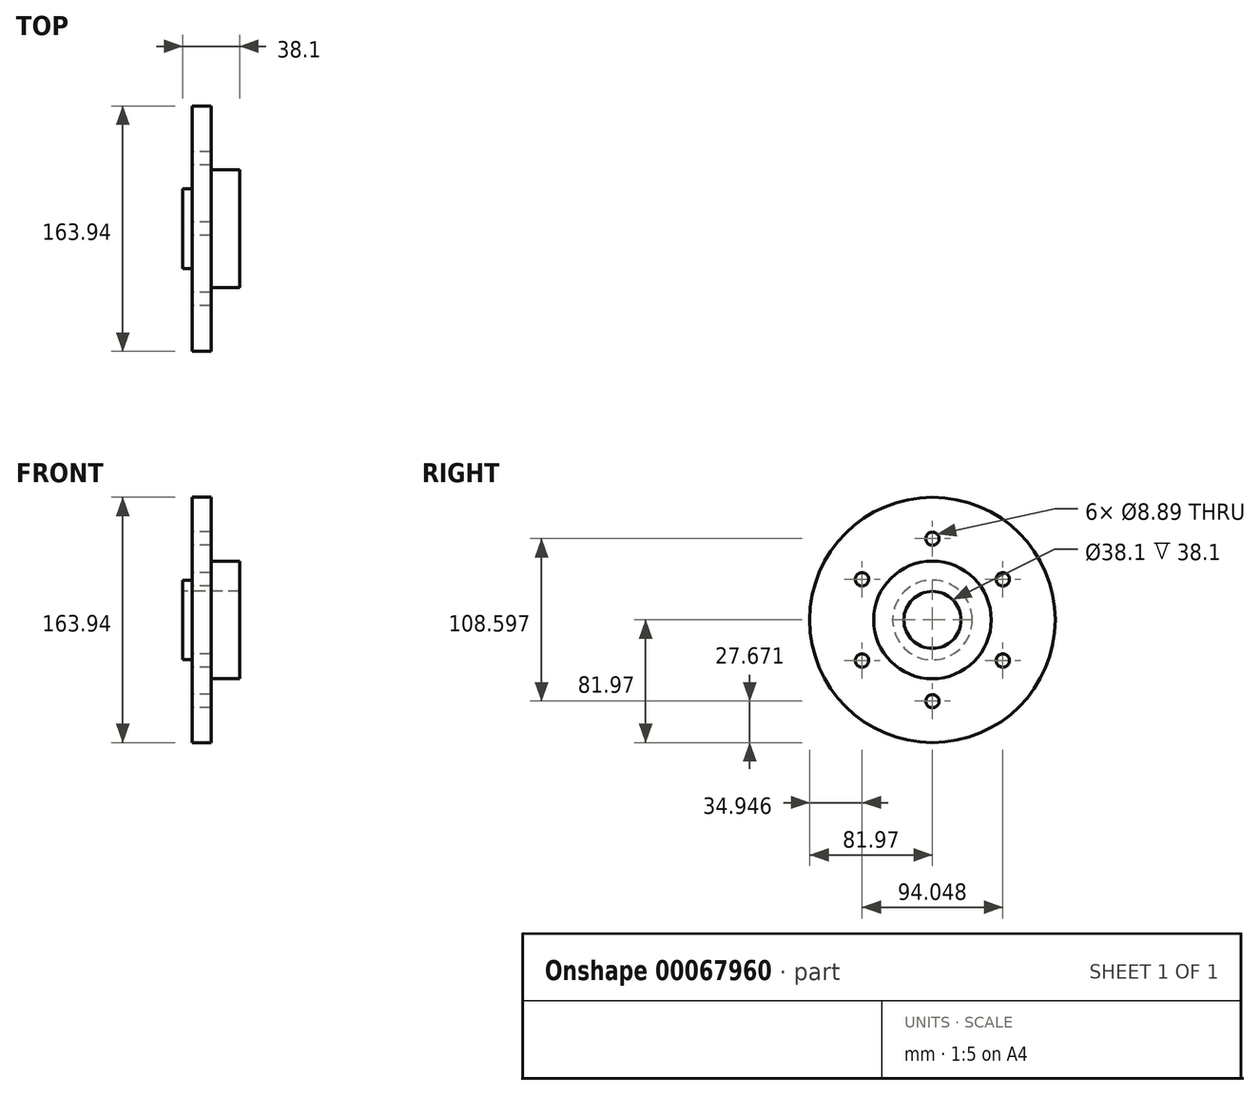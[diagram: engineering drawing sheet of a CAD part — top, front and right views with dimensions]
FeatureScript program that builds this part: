
annotation { "Feature Type Name" : "Feature", "Feature Type Description" : "" }
export const myFeature = defineFeature(function(context is Context, id is Id, definition is map)
    precondition{}
    {
        {
            var Q0;
            Q0=qCreatedBy(makeId("Front.planeOp"),FACE);
            var sketch = newSketch(context, id + "F0", { "sketchPlane" : qUnion([Q0])});
            skLineSegment(sketch, "E0", {"start": v(-89.12, 0) * mm, "end": v(94.02, 0) * mm, "construction": true});
            skLineSegment(sketch, "E1", {"start": v(0, 19.05) * mm, "end": v(38.1, 19.05) * mm});
            skLineSegment(sketch, "E2", {"start": v(38.1, 19.05) * mm, "end": v(38.1, 39.29) * mm});
            skLineSegment(sketch, "E3", {"start": v(38.1, 39.29) * mm, "end": v(19.05, 39.29) * mm});
            skLineSegment(sketch, "E4", {"start": v(19.05, 39.29) * mm, "end": v(19.05, 81.97) * mm});
            skLineSegment(sketch, "E5", {"start": v(19.05, 81.97) * mm, "end": v(6.35, 81.97) * mm});
            skLineSegment(sketch, "E6", {"start": v(6.35, 81.97) * mm, "end": v(6.35, 26.63) * mm});
            skLineSegment(sketch, "E7", {"start": v(6.35, 26.63) * mm, "end": v(0, 26.63) * mm});
            skLineSegment(sketch, "E8", {"start": v(0, 26.63) * mm, "end": v(0, 19.05) * mm});
            skPoint(sketch, "E9", {"position": v(6.35, 54.3) * mm});
            skSolve(sketch);
        }
        {
            var Q0;
            Q0=makeQuery(id+"F0.imprint","IMPRINT",FACE,{"disambiguationData":[TD([[makeQuery(id+"F0.imprint","IMPRINT",EDGE,{"derivedFrom":sQuery(id+"F0.wireOp",EDGE,"E1")}),1.0]])]});
            var Q1;
            Q1=sQuery(id+"F0.wireOp",EDGE,"E0");
            revolve(context, id + "F1", {"entities" : qUnion([Q0]), "axis" : qUnion([Q1]), "revolveType" : RevolveType.FULL});
        }
        {
            var Q0;
            Q0=makeQuery(id+"F1.opRevolve","SWEPT_FACE",FACE,{"disambiguationData":[OSD([sQuery(id+"F0.wireOp",EDGE,"E6")])]});
            var Q1;
            Q1 = qBodyType(qCreatedBy(id + "F3" ,EDGE), BodyType.WIRE);
            cPlane(context, id + "F2", {"entities" : qUnion([Q0, Q1]), "cplaneType" : CPlaneType.OFFSET, "offset" : 0 * mm, "width" : 152.4 * mm, "height" : 152.4 * mm});
        }
        {
            var Q0;
            Q0=qCreatedBy(id+"F2.planeOp",FACE);
            var sketch = newSketch(context, id + "F3", { "sketchPlane" : qUnion([Q0])});
            skCircle(sketch, "E10", {"center": v(0, 0) * mm, "radius": 54.3 * mm, "construction": true});
            skCircle(sketch, "E11", {"center": v(0, 54.3) * mm, "radius": 4.45 * mm});
            skCircle(sketch, "E12.1.0", {"center": v(-47.02, 27.15) * mm, "radius": 4.45 * mm});
            skCircle(sketch, "E12.2.0", {"center": v(-47.02, -27.15) * mm, "radius": 4.45 * mm});
            skCircle(sketch, "E12.3.0", {"center": v(0, -54.3) * mm, "radius": 4.45 * mm});
            skCircle(sketch, "E12.4.0", {"center": v(47.02, -27.15) * mm, "radius": 4.45 * mm});
            skCircle(sketch, "E12.5.0", {"center": v(47.02, 27.15) * mm, "radius": 4.45 * mm});
            skSolve(sketch);
        }
        {
            var Q0;
            Q0=makeQuery(id+"F3.imprint","IMPRINT",FACE,{"disambiguationData":[TD([[makeQuery(id+"F3.imprint","IMPRINT",EDGE,{"derivedFrom":sQuery(id+"F3.wireOp",EDGE,"E11")}),1.0]])]});
            var Q1;
            Q1=makeQuery(id+"F3.imprint","IMPRINT",FACE,{"disambiguationData":[TD([[makeQuery(id+"F3.imprint","IMPRINT",EDGE,{"derivedFrom":sQuery(id+"F3.wireOp",EDGE,"E12.1.0")}),1.0]])]});
            var Q2;
            Q2=makeQuery(id+"F3.imprint","IMPRINT",FACE,{"disambiguationData":[TD([[makeQuery(id+"F3.imprint","IMPRINT",EDGE,{"derivedFrom":sQuery(id+"F3.wireOp",EDGE,"E12.2.0")}),1.0]])]});
            var Q3;
            Q3=makeQuery(id+"F3.imprint","IMPRINT",FACE,{"disambiguationData":[TD([[makeQuery(id+"F3.imprint","IMPRINT",EDGE,{"derivedFrom":sQuery(id+"F3.wireOp",EDGE,"E12.3.0")}),1.0]])]});
            var Q4;
            Q4=makeQuery(id+"F3.imprint","IMPRINT",FACE,{"disambiguationData":[TD([[makeQuery(id+"F3.imprint","IMPRINT",EDGE,{"derivedFrom":sQuery(id+"F3.wireOp",EDGE,"E12.4.0")}),1.0]])]});
            var Q5;
            Q5=makeQuery(id+"F3.imprint","IMPRINT",FACE,{"disambiguationData":[TD([[makeQuery(id+"F3.imprint","IMPRINT",EDGE,{"derivedFrom":sQuery(id+"F3.wireOp",EDGE,"E12.5.0")}),1.0]])]});
            extrude(context, id + "F4", {"entities" : qUnion([Q0, Q1, Q2, Q3, Q4, Q5]), "operationType" : NewBodyOperationType.REMOVE, "endBound" : BoundingType.THROUGH_ALL, "oppositeDirection" : true, "depth" : 25.4 * mm});
        }
    });
